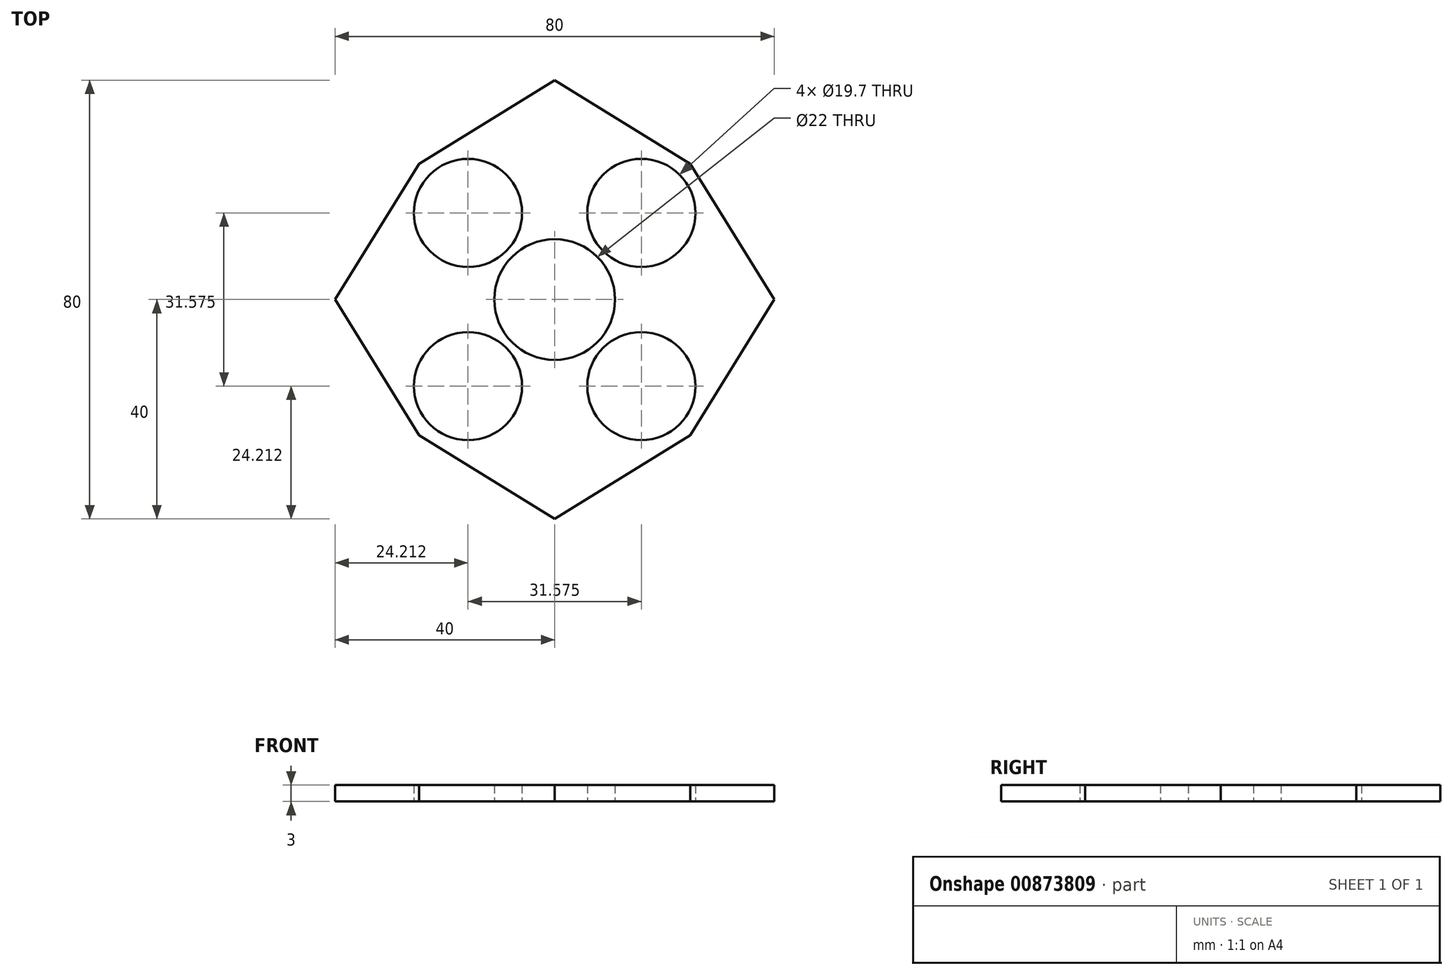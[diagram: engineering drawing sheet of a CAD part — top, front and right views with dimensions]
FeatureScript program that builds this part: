
annotation { "Feature Type Name" : "Feature", "Feature Type Description" : "" }
export const myFeature = defineFeature(function(context is Context, id is Id, definition is map)
    precondition{}
    {
        {
            var Q0;
            Q0=qCreatedBy(makeId("Top.planeOp"),FACE);
            var sketch = newSketch(context, id + "F0", { "sketchPlane" : qUnion([Q0])});
            skCircle(sketch, "E0", {"center": v(0, 0) * mm, "radius": 11 * mm});
            skLineSegment(sketch, "E1", {"start": v(0, 40) * mm, "end": v(-24.72, 24.72) * mm});
            skLineSegment(sketch, "E2", {"start": v(-24.72, 24.72) * mm, "end": v(-40, 0) * mm});
            skCircle(sketch, "E3", {"center": v(-15.79, 15.79) * mm, "radius": 9.85 * mm});
            skCircle(sketch, "E4.1.3", {"center": v(-15.79, -15.79) * mm, "radius": 9.85 * mm});
            skLineSegment(sketch, "E4.1.5", {"start": v(-24.72, -24.72) * mm, "end": v(0, -40) * mm});
            skLineSegment(sketch, "E4.1.6", {"start": v(-40, 0) * mm, "end": v(-24.72, -24.72) * mm});
            skCircle(sketch, "E4.2.3", {"center": v(15.79, -15.79) * mm, "radius": 9.85 * mm});
            skLineSegment(sketch, "E4.2.5", {"start": v(24.72, -24.72) * mm, "end": v(40, 0) * mm});
            skLineSegment(sketch, "E4.2.6", {"start": v(0, -40) * mm, "end": v(24.72, -24.72) * mm});
            skCircle(sketch, "E4.3.3", {"center": v(15.79, 15.79) * mm, "radius": 9.85 * mm});
            skLineSegment(sketch, "E4.3.5", {"start": v(24.72, 24.72) * mm, "end": v(0, 40) * mm});
            skLineSegment(sketch, "E4.3.6", {"start": v(40, 0) * mm, "end": v(24.72, 24.72) * mm});
            skSolve(sketch);
        }
        {
            var Q0;
            Q0 = qSketchRegion(id + "F0", true);
            extrude(context, id + "F1", {"entities" : qUnion([Q0]), "depth" : 3 * mm, "offsetDistance" : 25 * mm});
        }
    });
